# Revit family: Indoor_Pendant Lamp_Santa&Cole_Nimba
name_source: partatom
category: Luminarias
revit_build: Autodesk Revit 2018 (Build: 20190510_1515(x64)
units: mm (PartAtom-declared; Revit-internal decimal feet)

## family parameters
Anfitrión = Cara
Compartido = No
Corte con vacíos al cargar = No
Cota de conector redondo = Diámetro de uso
Origen de luz = Sí
Punto de cálculo de habitación = No
Tipo de pieza = Normal

## types (4) — shared parameters
Assembly Instructions - CE = https://www.santacole.com
Assembly Instructions - UL = https://www.santacole.com
Cambio de temperatura de color de luz atenuada = <Ninguno>
Elevación por defecto = 121.92 cm
Energy Label = https://www.santacole.com
Fabricante = Santa & Cole
Filtro de color = 16777215
Lamp Shade Height = 7.43 cm
Lámpara = LED STRIP
Manufacturer website = http://www.santacole.com
Modelo = Nimba
Technical Information = https://www.santacole.com
URL = https://www.santacole.com
Voltaje (90-305 V) = 220 V
Ángulo de inclinación = 90.00°

## per-type parameters (varying)
| type | Archivo de red fotométrica | Carga aparente | Code | Junction_120 | Junction_60 | Junction_90 | Juntion_180 | Lampshade_Type | Load | Rossette_Type | Structure_Type | Weight |
| Nimba 60 | NIM06LED.IES | 45 W | NIM06x | No | Sí | No | No | Lampshade : PlasticLampshade_Nimba60 | 45 W | CircularCeilingPlate : CircularCeilingPlate_J=3 | StainsteelStructure : Structure_Nimba60 | 7.40 kg |
| Nimba 120 | NIM12LED.IES | 95 W | NIM12x | Sí | No | No | No | Lampshade : PlasticLampshade_Nimba120 | 95 W | CircularCeilingPlate : CircularCeilingPlate_J=4 | StainsteelStructure : Structure_Nimba120 | 12.60 kg |
| Nimba 180 | NIM18LED.IES | 140 W | NIM18x | No | No | No | Sí | Lampshade : PlasticLampshade_Nimba180 | 140 W | CircularCeilingPlate : CircularCeilingPlate_J=6 | StainsteelStructure : Structure_Nimba180 | 17.00 kg |
| Nimba 90 | NIM09LED.IES | 65 W | NIM09x | No | No | Sí | No | Lampshade : PlasticLampshade_Nimba90 | 65 W | CircularCeilingPlate : CircularCeilingPlate_J=3 | StainsteelStructure : Structure_Nimba90 | 9.50 kg |

## geometry (parser evidence)
native form markers: Blend x6, Sweep x10
no freeform markers — native parametric forms only
